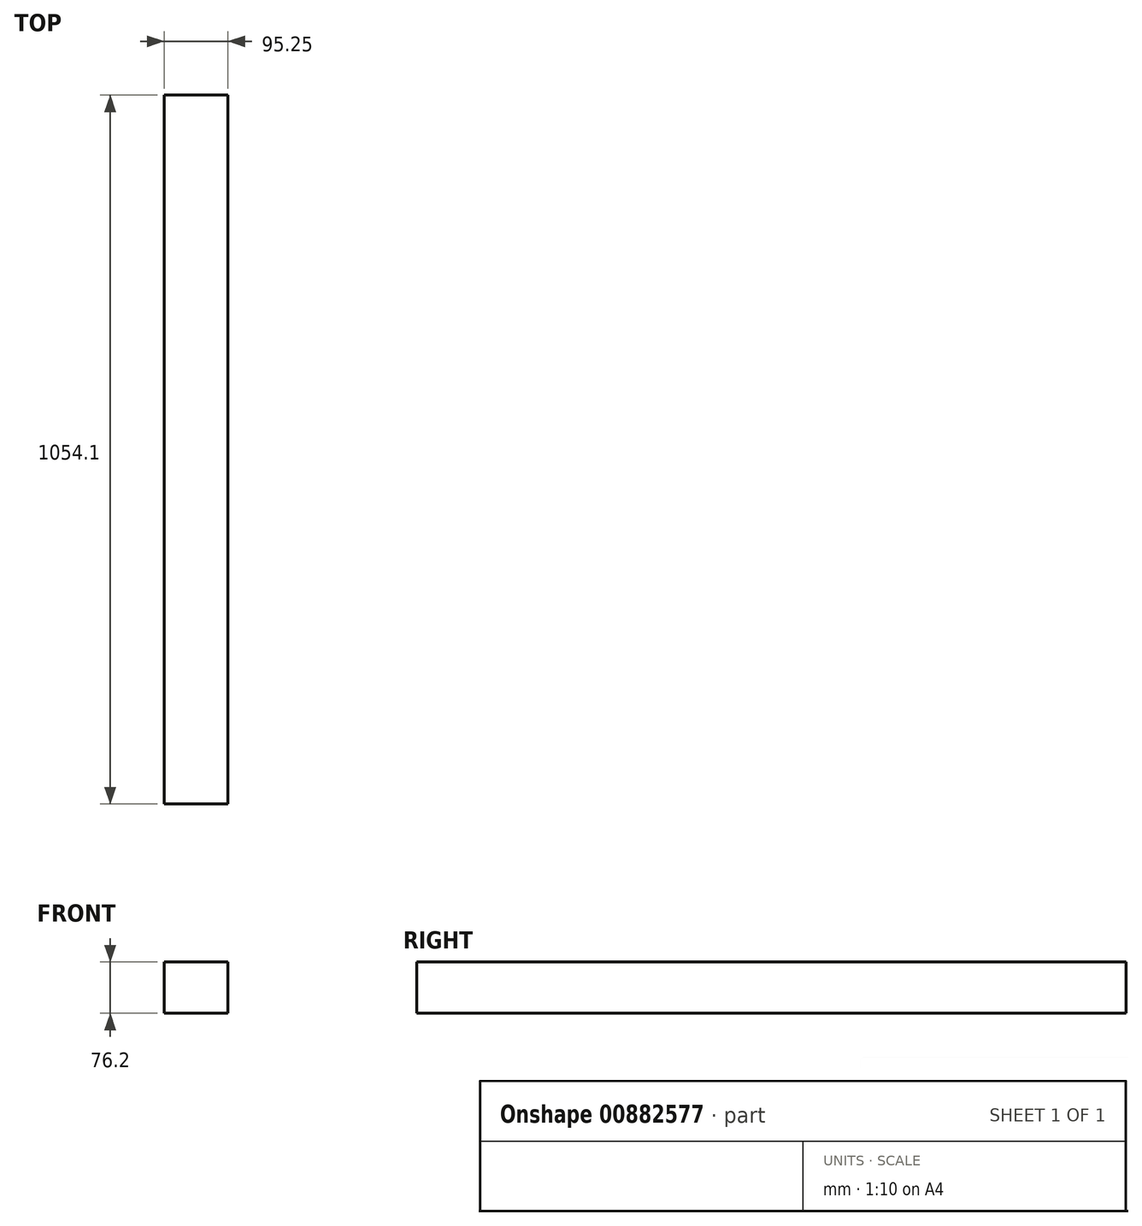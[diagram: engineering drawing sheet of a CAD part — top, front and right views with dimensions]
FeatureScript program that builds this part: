
annotation { "Feature Type Name" : "Feature", "Feature Type Description" : "" }
export const myFeature = defineFeature(function(context is Context, id is Id, definition is map)
    precondition{}
    {
        {
            var Q0;
            Q0=qCreatedBy(makeId("Front.planeOp"),FACE);
            var sketch = newSketch(context, id + "F0", { "sketchPlane" : qUnion([Q0])});
            skLineSegment(sketch, "E0.bottom", {"start": v(0, 0) * mm, "end": v(95.25, 0) * mm});
            skLineSegment(sketch, "E0.top", {"start": v(0, -76.2) * mm, "end": v(95.25, -76.2) * mm});
            skLineSegment(sketch, "E0.left", {"start": v(0, 0) * mm, "end": v(0, -76.2) * mm});
            skLineSegment(sketch, "E0.right", {"start": v(95.25, 0) * mm, "end": v(95.25, -76.2) * mm});
            skSolve(sketch);
        }
        {
            var Q0;
            Q0 = qSketchRegion(id + "F0", true);
            extrude(context, id + "F1", {"entities" : qUnion([Q0]), "depth" : 1054.1 * mm, "offsetDistance" : 25.4 * mm});
        }
    });
